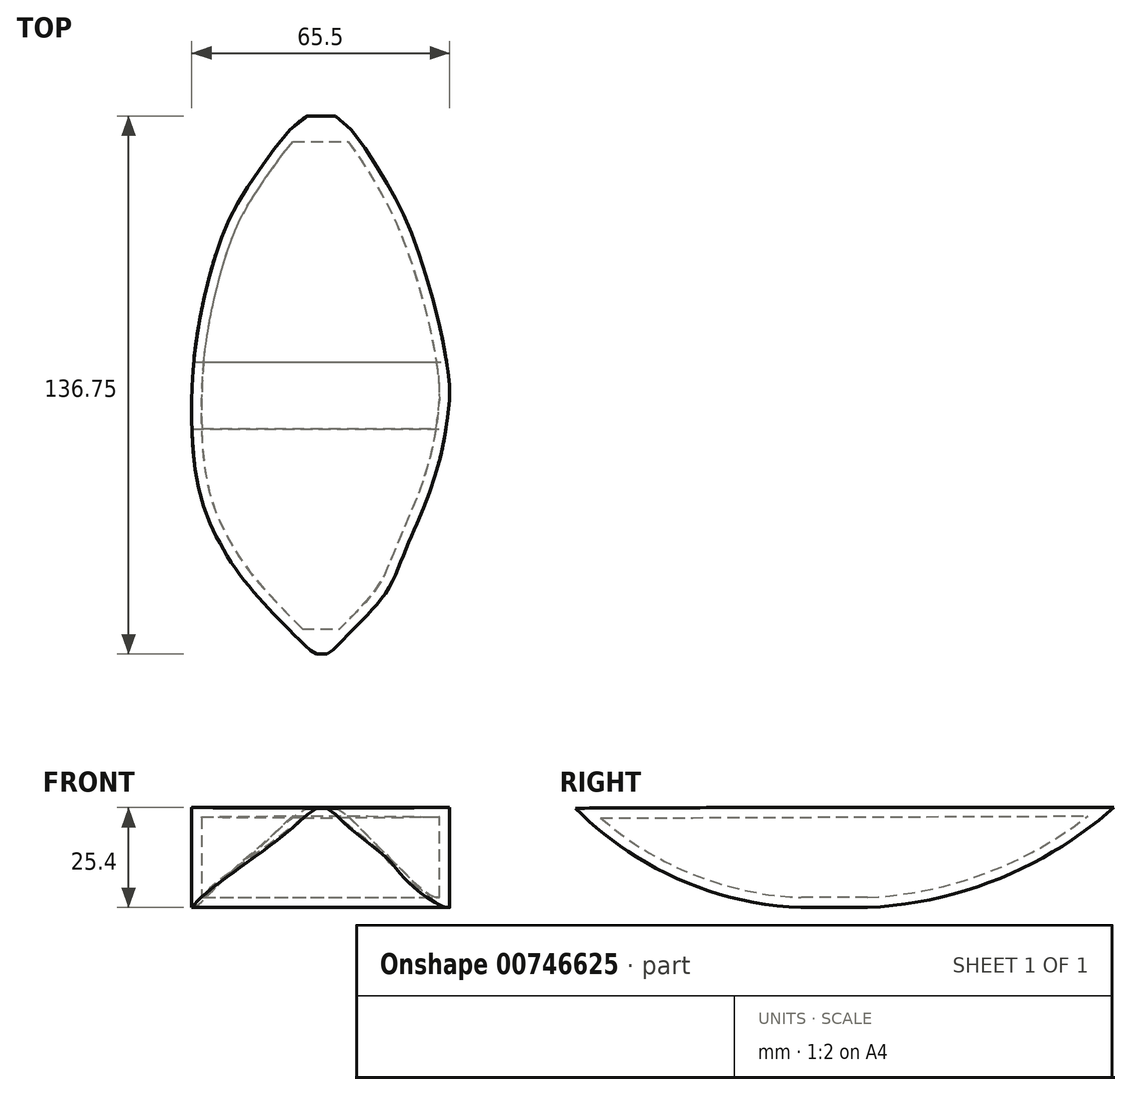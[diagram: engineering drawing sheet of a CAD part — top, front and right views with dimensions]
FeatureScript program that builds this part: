
annotation { "Feature Type Name" : "Feature", "Feature Type Description" : "" }
export const myFeature = defineFeature(function(context is Context, id is Id, definition is map)
    precondition{}
    {
        {
            var Q0;
            Q0=qCreatedBy(makeId("Top.planeOp"),FACE);
            var sketch = newSketch(context, id + "F0", { "sketchPlane" : qUnion([Q0])});
            skSolve(sketch);
        }
        {
            var Q0;
            Q0=qCreatedBy(makeId("Top.planeOp"),FACE);
            var sketch = newSketch(context, id + "F1", { "sketchPlane" : qUnion([Q0])});
            skFitSpline(sketch, "E0", {"points": [v(0, 73.44) * mm, v(-15.91, 58.84) * mm, v(-24.38, 44.53) * mm, v(-29.93, 26.43) * mm, v(-32.56, 10.95) * mm, v(-33.14, 0) * mm, v(-32.85, -11.83) * mm, v(-30.22, -26.72) * mm, v(-24.38, -38.98) * mm, v(-17.37, -48.62) * mm, v(-6.57, -60) * mm, v(0, -64.68) * mm, v(5.7, -60.3) * mm, v(15.62, -49.5) * mm, v(20, -40.74) * mm, v(24.67, -29.64) * mm, v(29.35, -16.8) * mm, v(32.27, 0) * mm, v(31.68, 9.2) * mm, v(28.18, 25.55) * mm, v(20.88, 46.87) * mm, v(13.58, 60) * mm, v(0, 73.44) * mm]});
            skSolve(sketch);
        }
        {
            var Q0;
            Q0 = qSketchRegion(id + "F0", true);
            var Q1;
            Q1=makeQuery(id+"F1.imprint","IMPRINT",FACE,{"disambiguationData":[TD([[makeQuery(id+"F1.imprint","IMPRINT",EDGE,{"derivedFrom":sQuery(id+"F1.wireOp",EDGE,"E0")}),1.0]])]});
            extrude(context, id + "F2", {"entities" : qUnion([Q0, Q1]), "depth" : 25.4 * mm, "offsetDistance" : 25.4 * mm});
        }
        {
            var Q0;
            Q0=qCreatedBy(makeId("Right.planeOp"),FACE);
            var sketch = newSketch(context, id + "F3", { "sketchPlane" : qUnion([Q0])});
            skArc(sketch, "E1", {"start": v(0, 0) * mm, "mid": v(38.99, 5.74) * mm, "end": v(72.88, 25.84) * mm});
            skArc(sketch, "E2", {"start": v(-64.36, 25.26) * mm, "mid": v(-34.84, 5.85) * mm, "end": v(0, 0) * mm});
            skLineSegment(sketch, "E3", {"start": v(-64.36, 25.26) * mm, "end": v(72.88, 25.84) * mm});
            skSolve(sketch);
        }
        {
            var Q0;
            Q0=makeQuery(id+"F3.imprint","IMPRINT",FACE,{"disambiguationData":[TD([[makeQuery(id+"F3.imprint","IMPRINT",EDGE,{"derivedFrom":sQuery(id+"F3.wireOp",EDGE,"E1")}),1.0]])]});
            extrude(context, id + "F4", {"entities" : qUnion([Q0]), "operationType" : NewBodyOperationType.INTERSECT, "endBound" : BoundingType.SYMMETRIC, "oppositeDirection" : true, "depth" : 179.32 * mm, "offsetDistance" : 25.4 * mm});
        }
        {
            var Q0;
            Q0=makeQuery(id+"F2.opExtrude","CAP_FACE",FACE,{"disambiguationData":[OSD([sQuery(id+"F1.wireOp",EDGE,"E0")])],"isStart":false});
            var Q1;
            Q1=makeQuery(id+"F4.boolean.opBoolean","COPY",FACE,{"derivedFrom":makeQuery(id+"F4.boolean.toolComplement.opBoolean","COPY",FACE,{"derivedFrom":makeQuery(id+"F4.opExtrude","SWEPT_FACE",FACE,{"disambiguationData":[OSD([sQuery(id+"F3.wireOp",EDGE,"E3")])]})})});
            shell(context, id + "F5", {"entities" : qUnion([Q0, Q1]), "thickness" : 2.54 * mm});
        }
    });
